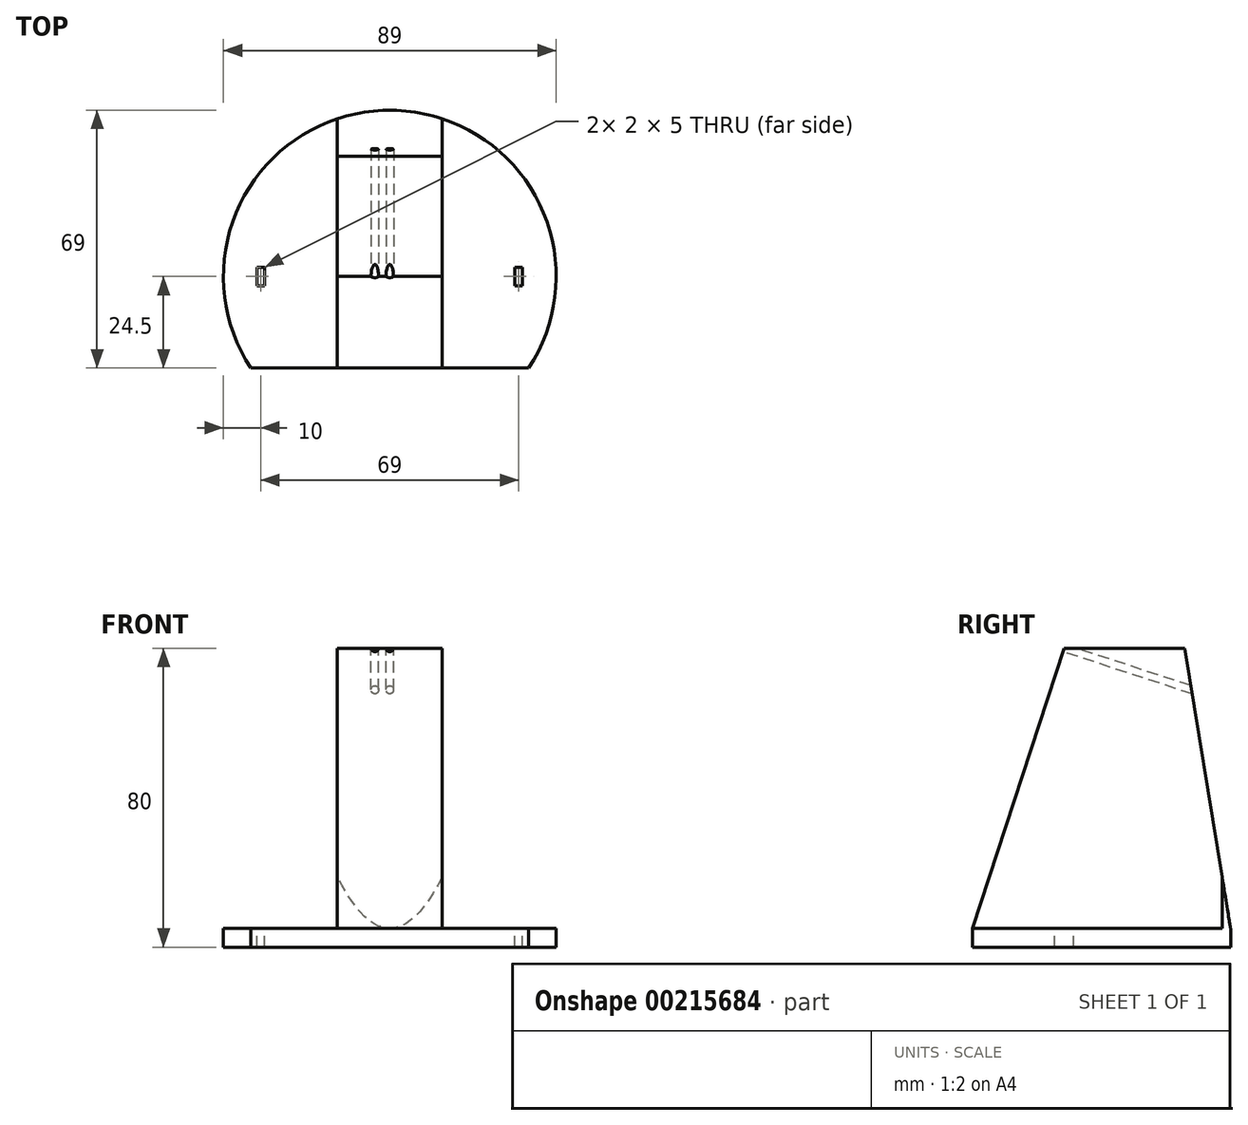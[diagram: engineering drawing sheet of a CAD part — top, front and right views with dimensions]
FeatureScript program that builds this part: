
annotation { "Feature Type Name" : "Feature", "Feature Type Description" : "" }
export const myFeature = defineFeature(function(context is Context, id is Id, definition is map)
    precondition{}
    {
        {
            var Q0;
            Q0=qCreatedBy(makeId("Top.planeOp"),FACE);
            var sketch = newSketch(context, id + "F0", { "sketchPlane" : qUnion([Q0])});
            skArc(sketch, "E0", {"start": v(-31.94, -15.5) * mm, "mid": v(0, 35.5) * mm, "end": v(31.94, -15.5) * mm, "construction": true});
            skLineSegment(sketch, "E1", {"start": v(-31.94, -15.5) * mm, "end": v(31.94, -15.5) * mm, "construction": true});
            skArc(sketch, "E2", {"start": v(-37.15, -24.5) * mm, "mid": v(0, 44.5) * mm, "end": v(37.15, -24.5) * mm});
            skLineSegment(sketch, "E3", {"start": v(-37.15, -24.5) * mm, "end": v(37.15, -24.5) * mm});
            skSolve(sketch);
        }
        {
            var Q0;
            Q0 = qSketchRegion(id + "F0", true);
            extrude(context, id + "F1", {"entities" : qUnion([Q0]), "depth" : 5 * mm});
        }
        {
            var Q0;
            Q0=makeQuery(id+"F1.opExtrude","CAP_FACE",FACE,{"disambiguationData":[OSD([sQuery(id+"F0.wireOp",EDGE,"E2"),sQuery(id+"F0.wireOp",EDGE,"E3")])],"isStart":false});
            var sketch = newSketch(context, id + "F2", { "sketchPlane" : qUnion([Q0])});
            skLineSegment(sketch, "E4", {"start": v(0, -24.5) * mm, "end": v(-14, -24.5) * mm});
            skLineSegment(sketch, "E5", {"start": v(-14, -24.5) * mm, "end": v(-14, 42.24) * mm});
            skArc(sketch, "E6", {"start": v(-14, 42.24) * mm, "mid": v(0, 44.5) * mm, "end": v(14, 42.24) * mm});
            skLineSegment(sketch, "E7", {"start": v(14, 42.24) * mm, "end": v(14, -24.5) * mm});
            skLineSegment(sketch, "E8", {"start": v(14, -24.5) * mm, "end": v(0, -24.5) * mm});
            skSolve(sketch);
        }
        {
            var Q0;
            Q0 = qSketchRegion(id + "F2", true);
            extrude(context, id + "F3", {"entities" : qUnion([Q0]), "operationType" : NewBodyOperationType.ADD, "depth" : 75 * mm});
        }
        {
            var Q0;
            Q0=makeQuery(id+"F3.opExtrude","SWEPT_FACE",FACE,{"disambiguationData":[OSD([sQuery(id+"F2.wireOp",EDGE,"E7")])]});
            var sketch = newSketch(context, id + "F4", { "sketchPlane" : qUnion([Q0])});
            skLineSegment(sketch, "E9", {"start": v(0, 80) * mm, "end": v(-24.5, 5) * mm});
            skLineSegment(sketch, "E10", {"start": v(-24.5, 5) * mm, "end": v(-35, 5) * mm});
            skLineSegment(sketch, "E11", {"start": v(-35, 5) * mm, "end": v(-35, 88) * mm});
            skLineSegment(sketch, "E12", {"start": v(0, 80) * mm, "end": v(0, 88) * mm});
            skLineSegment(sketch, "E13", {"start": v(0, 88) * mm, "end": v(-35, 88) * mm});
            skLineSegment(sketch, "E14", {"start": v(32.21, 88) * mm, "end": v(57.21, 88) * mm});
            skLineSegment(sketch, "E15", {"start": v(57.21, 88) * mm, "end": v(57.21, 5) * mm});
            skLineSegment(sketch, "E16", {"start": v(57.21, 5) * mm, "end": v(44.5, 5) * mm});
            skLineSegment(sketch, "E17", {"start": v(44.5, 5) * mm, "end": v(32.21, 80) * mm});
            skLineSegment(sketch, "E18", {"start": v(32.21, 80) * mm, "end": v(32.21, 88) * mm});
            skSolve(sketch);
        }
        {
            var Q0;
            Q0 = qSketchRegion(id + "F4", true);
            extrude(context, id + "F5", {"entities" : qUnion([Q0]), "operationType" : NewBodyOperationType.REMOVE, "endBound" : BoundingType.THROUGH_ALL, "oppositeDirection" : true, "depth" : 25 * mm});
        }
        {
            var Q0;
            {var subQ0=sQuery(id+"F0.wireOp",EDGE,"E3");var subQ1=sQuery(id+"F0.wireOp",EDGE,"E2");Q0=makeQuery(id+"F3.boolean.opBoolean","SPLIT",FACE,{"disambiguationData":[TD([makeQuery(id+"F3.opExtrude","SWEPT_FACE",FACE,{"disambiguationData":[OSD([sQuery(id+"F2.wireOp",EDGE,"E5")])]})])],"derivedFrom":makeQuery(id+"F1.opExtrude","CAP_FACE",FACE,{"disambiguationData":[OSD([subQ1,subQ0])],"isStart":false})});}
            var sketch = newSketch(context, id + "F6", { "sketchPlane" : qUnion([Q0])});
            skCircle(sketch, "E19", {"center": v(0, 0) * mm, "radius": 33.5 * mm, "construction": true});
            skLineSegment(sketch, "E20", {"start": v(-33.5, 0) * mm, "end": v(-33.5, 2.5) * mm});
            skLineSegment(sketch, "E21", {"start": v(-33.5, 2.5) * mm, "end": v(-35.5, 2.5) * mm});
            skLineSegment(sketch, "E22", {"start": v(-35.5, 2.5) * mm, "end": v(-35.5, -2.5) * mm});
            skLineSegment(sketch, "E23", {"start": v(-35.5, -2.5) * mm, "end": v(-33.5, -2.5) * mm});
            skLineSegment(sketch, "E24", {"start": v(-33.5, -2.5) * mm, "end": v(-33.5, 0) * mm});
            skLineSegment(sketch, "E25.MirrorCS", {"start": v(33.5, 2.5) * mm, "end": v(35.5, 2.5) * mm});
            skLineSegment(sketch, "E26.MirrorCS", {"start": v(35.5, 2.5) * mm, "end": v(35.5, -2.5) * mm});
            skLineSegment(sketch, "E27.MirrorCS", {"start": v(35.5, -2.5) * mm, "end": v(33.5, -2.5) * mm});
            skLineSegment(sketch, "E28.MirrorCS", {"start": v(33.5, -2.5) * mm, "end": v(33.5, 0) * mm});
            skLineSegment(sketch, "E29.MirrorCS", {"start": v(33.5, 0) * mm, "end": v(33.5, 2.5) * mm});
            skSolve(sketch);
        }
        {
            var Q0;
            Q0 = qSketchRegion(id + "F6", true);
            extrude(context, id + "F7", {"entities" : qUnion([Q0]), "operationType" : NewBodyOperationType.REMOVE, "endBound" : BoundingType.THROUGH_ALL, "oppositeDirection" : true, "depth" : 25 * mm});
        }
        {
            var Q0;
            Q0=makeQuery(id+"F5.boolean.opBoolean","COPY",FACE,{"derivedFrom":makeQuery(id+"F5.opExtrude","SWEPT_FACE",FACE,{"disambiguationData":[OSD([sQuery(id+"F4.wireOp",EDGE,"E9")])]})});
            var sketch = newSketch(context, id + "F8", { "sketchPlane" : qUnion([Q0])});
            skCircle(sketch, "E30", {"center": v(0, 76.05) * mm, "radius": 1 * mm});
            skCircle(sketch, "E31", {"center": v(-4, 76.05) * mm, "radius": 1 * mm});
            skSolve(sketch);
        }
        {
            var Q0;
            Q0 = qSketchRegion(id + "F8", true);
            extrude(context, id + "F9", {"entities" : qUnion([Q0]), "operationType" : NewBodyOperationType.REMOVE, "endBound" : BoundingType.THROUGH_ALL, "oppositeDirection" : true, "depth" : 25 * mm});
        }
    });
